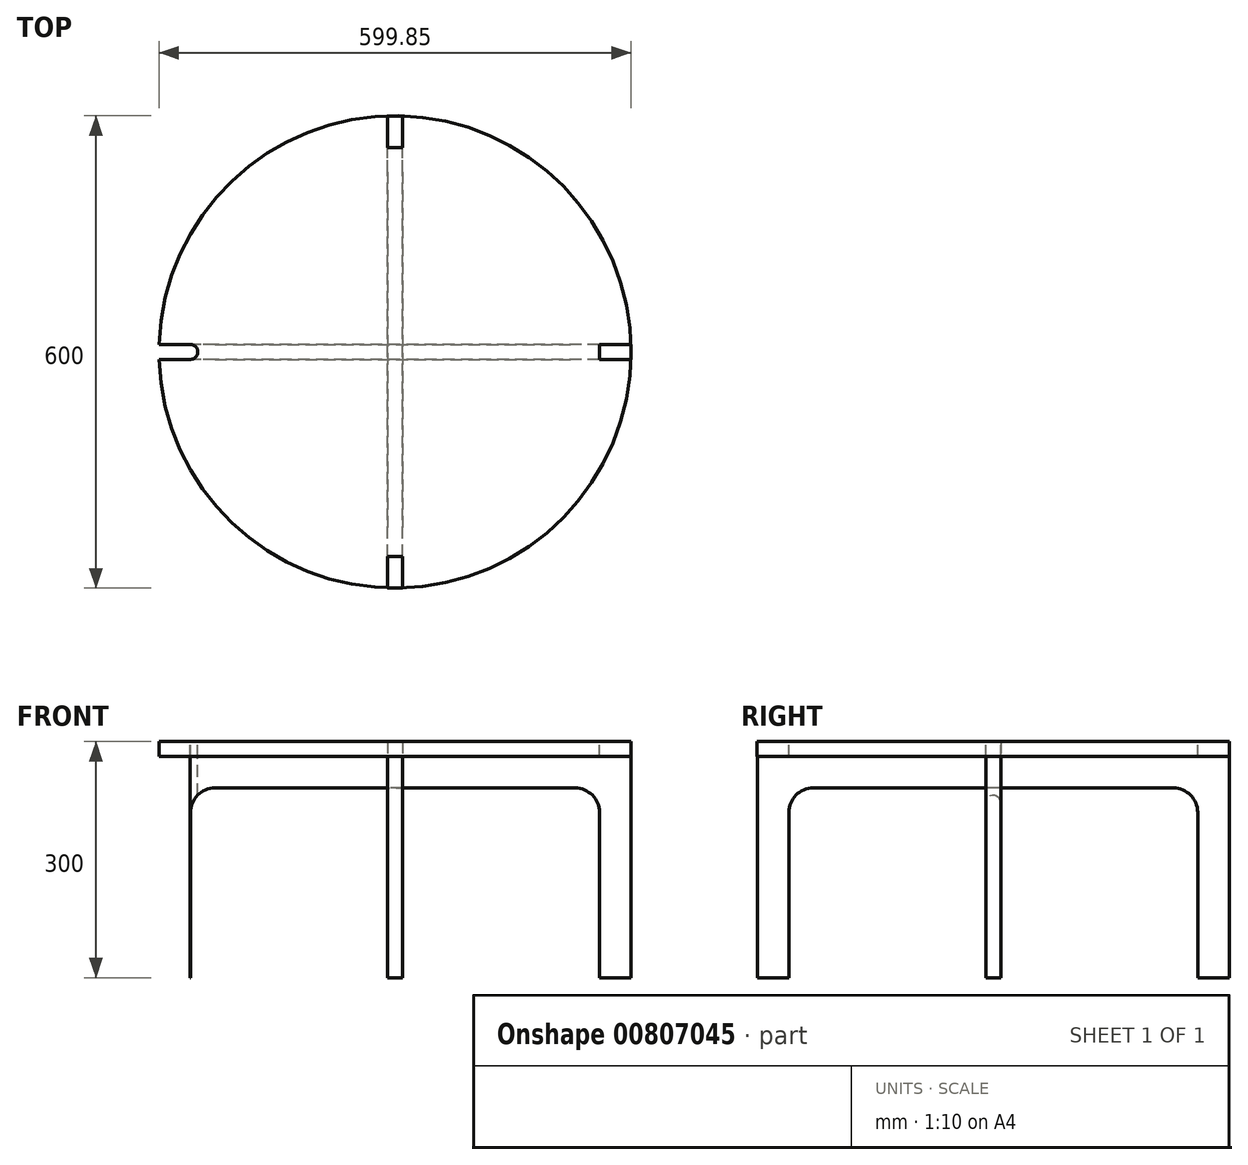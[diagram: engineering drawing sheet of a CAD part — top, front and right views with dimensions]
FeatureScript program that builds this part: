
annotation { "Feature Type Name" : "Feature", "Feature Type Description" : "" }
export const myFeature = defineFeature(function(context is Context, id is Id, definition is map)
    precondition{}
    {
        {
            var Q0;
            Q0=qCreatedBy(makeId("Top.planeOp"),FACE);
            var sketch = newSketch(context, id + "F0", { "sketchPlane" : qUnion([Q0])});
            skCircle(sketch, "E0", {"center": v(0, 0) * mm, "radius": 300 * mm});
            skSolve(sketch);
        }
        {
            var Q0;
            Q0 = qSketchRegion(id + "F0", true);
            extrude(context, id + "F1", {"entities" : qUnion([Q0]), "depth" : 19 * mm, "offsetDistance" : 25 * mm});
        }
        {
            var Q0;
            Q0=qCreatedBy(makeId("Front.planeOp"),FACE);
            var sketch = newSketch(context, id + "F2", { "sketchPlane" : qUnion([Q0])});
            skLineSegment(sketch, "E1", {"start": v(-299.71, 19) * mm, "end": v(-299.71, -281) * mm});
            skLineSegment(sketch, "E2", {"start": v(-299.71, -281) * mm, "end": v(-259.71, -281) * mm});
            skLineSegment(sketch, "E3", {"start": v(-259.71, -281) * mm, "end": v(-259.71, -40) * mm});
            skLineSegment(sketch, "E4", {"start": v(-259.71, -40) * mm, "end": v(0, -40) * mm});
            skLineSegment(sketch, "E5", {"start": v(0, -40) * mm, "end": v(0, 0) * mm});
            skLineSegment(sketch, "E6", {"start": v(0, 0) * mm, "end": v(-259.71, 0) * mm});
            skLineSegment(sketch, "E7", {"start": v(-259.71, 0) * mm, "end": v(-259.71, 19) * mm});
            skLineSegment(sketch, "E8", {"start": v(-259.71, 19) * mm, "end": v(-299.71, 19) * mm});
            skLineSegment(sketch, "E9.MirrorCS", {"start": v(259.71, 0) * mm, "end": v(259.71, 19) * mm});
            skLineSegment(sketch, "E10.MirrorCS", {"start": v(0, 0) * mm, "end": v(259.71, 0) * mm});
            skLineSegment(sketch, "E11.MirrorCS", {"start": v(259.71, 19) * mm, "end": v(299.71, 19) * mm});
            skLineSegment(sketch, "E12.MirrorCS", {"start": v(299.71, -281) * mm, "end": v(259.71, -281) * mm});
            skLineSegment(sketch, "E13.MirrorCS", {"start": v(259.71, -40) * mm, "end": v(0, -40) * mm});
            skLineSegment(sketch, "E14.MirrorCS", {"start": v(259.71, -281) * mm, "end": v(259.71, -40) * mm});
            skLineSegment(sketch, "E15.MirrorCS", {"start": v(299.71, 19) * mm, "end": v(299.71, -281) * mm});
            skSolve(sketch);
        }
        {
            var Q0;
            Q0 = qSketchRegion(id + "F2", true);
            extrude(context, id + "F3", {"entities" : qUnion([Q0]), "depth" : (19 / 2) * mm, "offsetDistance" : 25 * mm, "hasSecondDirection" : true, "secondDirectionOppositeDirection" : true, "secondDirectionDepth" : 9.5 * mm});
        }
        {
            var Q0;
            Q0=makeQuery(id+"F3.opExtrude","SWEPT_EDGE",EDGE,{"disambiguationData":[OSD([sQuery(id+"F2.wireOp",EDGE,"E3"),sQuery(id+"F2.wireOp",EDGE,"E4")])]});
            var Q1;
            Q1=makeQuery(id+"F3.opExtrude","SWEPT_EDGE",EDGE,{"disambiguationData":[OSD([sQuery(id+"F2.wireOp",EDGE,"E13.MirrorCS"),sQuery(id+"F2.wireOp",EDGE,"E14.MirrorCS")])]});
            fillet(context, id + "F4", {"entities" : qUnion([Q0, Q1]), "radius" : 31 * mm, "tangentPropagation" : true, "allowEdgeOverflow" : false});
        }
        {
            var Q0;
            Q0=qCreatedBy(makeId("Front.planeOp"),FACE);
            var Q1;
            Q1=qCreatedBy(makeId("Right.planeOp"),FACE);
            cPlane(context, id + "F5", {"entities" : qUnion([Q0, Q1]), "cplaneType" : CPlaneType.MID_PLANE, "offset" : 25 * mm, "width" : 150 * mm, "height" : 150 * mm});
        }
        {
            var Q0;
            Q0=makeQuery(id+"F3.opExtrude","SWEPT_BODY",BODY,{"disambiguationData":[OSD([sQuery(id+"F2.wireOp",EDGE,"E1"),sQuery(id+"F2.wireOp",EDGE,"E2"),sQuery(id+"F2.wireOp",EDGE,"E3"),sQuery(id+"F2.wireOp",EDGE,"E4"),sQuery(id+"F2.wireOp",EDGE,"E6"),sQuery(id+"F2.wireOp",EDGE,"E7"),sQuery(id+"F2.wireOp",EDGE,"E8"),sQuery(id+"F2.wireOp",EDGE,"E9.MirrorCS"),sQuery(id+"F2.wireOp",EDGE,"E10.MirrorCS"),sQuery(id+"F2.wireOp",EDGE,"E11.MirrorCS"),sQuery(id+"F2.wireOp",EDGE,"E12.MirrorCS"),sQuery(id+"F2.wireOp",EDGE,"E13.MirrorCS"),sQuery(id+"F2.wireOp",EDGE,"E14.MirrorCS"),sQuery(id+"F2.wireOp",EDGE,"E15.MirrorCS")])]});
            var Q1;
            Q1=qCreatedBy(id+"F5.planeOp",FACE);
            mirror(context, id + "F6", {"entities" : qUnion([Q0]), "mirrorPlane" : qUnion([Q1])});
        }
        {
            var Q0;
            Q0=makeQuery(id+"F1.opExtrude","CAP_FACE",FACE,{"disambiguationData":[OSD([sQuery(id+"F0.wireOp",EDGE,"E0")])],"isStart":false});
            var sketch = newSketch(context, id + "F7", { "sketchPlane" : qUnion([Q0])});
            skLineSegment(sketch, "E16.bottom", {"start": v(-260, -9.5) * mm, "end": v(-340, -9.5) * mm});
            skLineSegment(sketch, "E16.top", {"start": v(-260, 9.5) * mm, "end": v(-340, 9.5) * mm});
            skLineSegment(sketch, "E16.left", {"start": v(-260, -9.5) * mm, "end": v(-260, 9.5) * mm, "construction": true});
            skLineSegment(sketch, "E16.right", {"start": v(-340, -9.5) * mm, "end": v(-340, 9.5) * mm});
            skPoint(sketch, "E16.middle", {"position": v(-300, 0) * mm});
            skArc(sketch, "E17", {"start": v(-260, -9.5) * mm, "mid": v(-250.5, 0) * mm, "end": v(-260, 9.5) * mm});
            skSolve(sketch);
        }
        {
            var Q0;
            Q0 = qSketchRegion(id + "F7", true);
            extrude(context, id + "F8", {"entities" : qUnion([Q0]), "operationType" : NewBodyOperationType.REMOVE, "endBound" : BoundingType.THROUGH_ALL, "oppositeDirection" : true, "depth" : 25 * mm, "offsetDistance" : 25 * mm});
        }
    });
